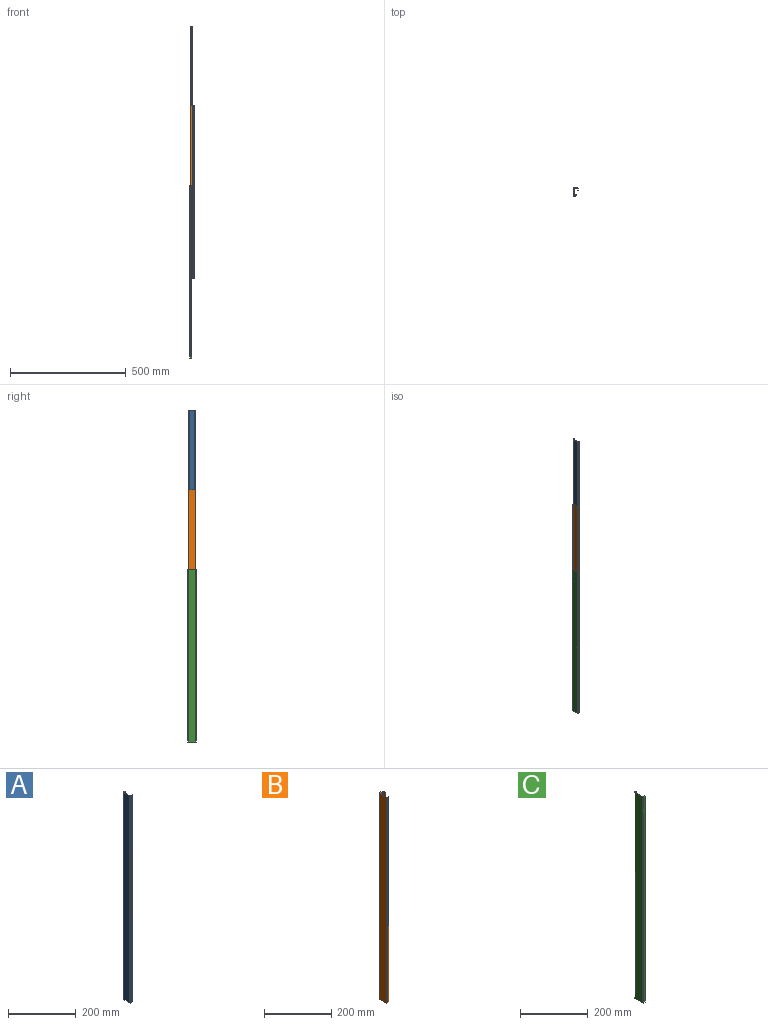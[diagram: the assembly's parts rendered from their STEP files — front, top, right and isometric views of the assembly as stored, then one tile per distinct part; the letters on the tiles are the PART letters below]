
ASSEMBLY  parts=3 mates=2
PART A: 14 faces, bbox 9x30x747 mm
  f0: cylinder r=1.5mm len=747mm, axis (0,0,-1), area 1760.1mm2, adj f1,f11,f12,f13
  f1: plane 747x6mm, normal (0,-1,0), area 4482mm2, adj f0,f2,f12,f13
  f2: plane 747x1.5mm, normal (1,0,0), area 1120.5mm2, adj f1,f3,f12,f13
  f3: plane 747x6mm, normal (0,1,0), area 4482mm2, adj f2,f4,f12,f13
  f4: cylinder r=3mm len=747mm, axis (0,0,-1), area 3520.2mm2, adj f3,f5,f12,f13
  f5: plane 747x24mm, normal (-1,0,0), area 17928mm2, adj f4,f6,f12,f13
  f6: cylinder r=3mm len=747mm, axis (0,0,-1), area 3520.2mm2, adj f5,f7,f12,f13
  f7: plane 747x6mm, normal (0,-1,0), area 4482mm2, adj f6,f8,f12,f13
  f8: plane 747x1.5mm, normal (1,0,0), area 1120.5mm2, adj f7,f9,f12,f13
  f9: plane 747x6mm, normal (0,1,0), area 4482mm2, adj f8,f10,f12,f13
  f10: cylinder r=1.5mm len=747mm, axis (0,0,-1), area 1760.1mm2, adj f9,f11,f12,f13
  f11: plane 747x24mm, normal (1,0,0), area 17928mm2, adj f0,f10,f12,f13
  f12: plane 30x9mm, normal (0,0,1), area 64.6mm2, adj f0,f1,f2,f3,f4,f5,f6,f7
  f13: plane 30x9mm, normal (0,0,-1), area 64.6mm2, adj f0,f1,f2,f3,f4,f5,f6,f7
PART B: 18 faces, bbox 17x33x747 mm
  f0: cylinder r=1mm len=747mm, axis (0,0,-1), area 1173.4mm2, adj f1,f15,f16,f17
  f1: plane 747x8.5mm, normal (-1,0,0), area 6349.5mm2, adj f0,f2,f16,f17
  f2: plane 747x1.5mm, normal (0,-1,0), area 1120.5mm2, adj f1,f3,f16,f17
  f3: plane 747x8.5mm, normal (1,0,0), area 6349.5mm2, adj f2,f4,f16,f17
  f4: cylinder r=2.5mm len=747mm, axis (0,0,-1), area 2933.5mm2, adj f3,f5,f16,f17
  f5: plane 747x12mm, normal (0,1,0), area 8964mm2, adj f4,f6,f16,f17
  f6: cylinder r=2.5mm len=747mm, axis (0,0,-1), area 2933.5mm2, adj f5,f7,f16,f17
  f7: plane 747x28mm, normal (-1,0,0), area 20916mm2, adj f6,f8,f16,f17
  f8: cylinder r=2.5mm len=747mm, axis (0,0,-1), area 2933.5mm2, adj f7,f9,f16,f17
  f9: plane 747x7mm, normal (0,-1,0), area 5229mm2, adj f8,f10,f16,f17
  f10: plane 747x1.5mm, normal (1,0,0), area 1120.5mm2, adj f9,f11,f16,f17
  f11: plane 747x7mm, normal (0,1,0), area 5229mm2, adj f10,f12,f16,f17
  f12: cylinder r=1mm len=747mm, axis (0,0,-1), area 1173.4mm2, adj f11,f13,f16,f17
  f13: plane 747x28mm, normal (1,0,0), area 20916mm2, adj f12,f14,f16,f17
  f14: cylinder r=1mm len=747mm, axis (0,0,-1), area 1173.4mm2, adj f13,f15,f16,f17
  f15: plane 747x12mm, normal (0,-1,0), area 8964mm2, adj f0,f14,f16,f17
  f16: plane 33x17mm, normal (0,0,1), area 95.6mm2, adj f0,f1,f2,f3,f4,f5,f6,f7
  f17: plane 33x17mm, normal (0,0,-1), area 95.6mm2, adj f0,f1,f2,f3,f4,f5,f6,f7
PART C: 14 faces, bbox 9x37x747 mm
  f0: plane 747x6mm, normal (0,1,0), area 4482mm2, adj f1,f11,f12,f13
  f1: cylinder r=1.5mm len=747mm, axis (0,0,-1), area 1760.1mm2, adj f0,f2,f12,f13
  f2: plane 747x31mm, normal (1,0,0), area 23157mm2, adj f1,f3,f12,f13
  f3: cylinder r=1.5mm len=747mm, axis (0,0,-1), area 1760.1mm2, adj f2,f4,f12,f13
  f4: plane 747x6mm, normal (0,-1,0), area 4482mm2, adj f3,f5,f12,f13
  f5: plane 747x1.5mm, normal (1,0,0), area 1120.5mm2, adj f4,f6,f12,f13
  f6: plane 747x6mm, normal (0,1,0), area 4482mm2, adj f5,f7,f12,f13
  f7: cylinder r=3mm len=747mm, axis (0,0,-1), area 3520.2mm2, adj f6,f8,f12,f13
  f8: plane 747x31mm, normal (-1,0,0), area 23157mm2, adj f7,f9,f12,f13
  f9: cylinder r=3mm len=747mm, axis (0,0,-1), area 3520.2mm2, adj f8,f10,f12,f13
  f10: plane 747x6mm, normal (0,-1,0), area 4482mm2, adj f9,f11,f12,f13
  f11: plane 747x1.5mm, normal (1,0,0), area 1120.5mm2, adj f0,f10,f12,f13
  f12: plane 37x9mm, normal (0,0,1), area 75.1mm2, adj f0,f1,f2,f3,f4,f5,f6,f7
  f13: plane 37x9mm, normal (0,0,-1), area 75.1mm2, adj f0,f1,f2,f3,f4,f5,f6,f7
PLACE A t=(-79.09,-0.69,580.35)mm
PLACE B t=(-80.59,-0.69,610.23)mm
PLACE C t=(-82.54,-0.69,266.62)mm fixed
MATE slider C.f12 <-> B.f16  axis (0,0,1) through (-80.42,-0.69,640.12)mm
MATE slider B.f16 <-> A.f12  axis (0,0,1) through (-75.04,2.5,983.73)mm
